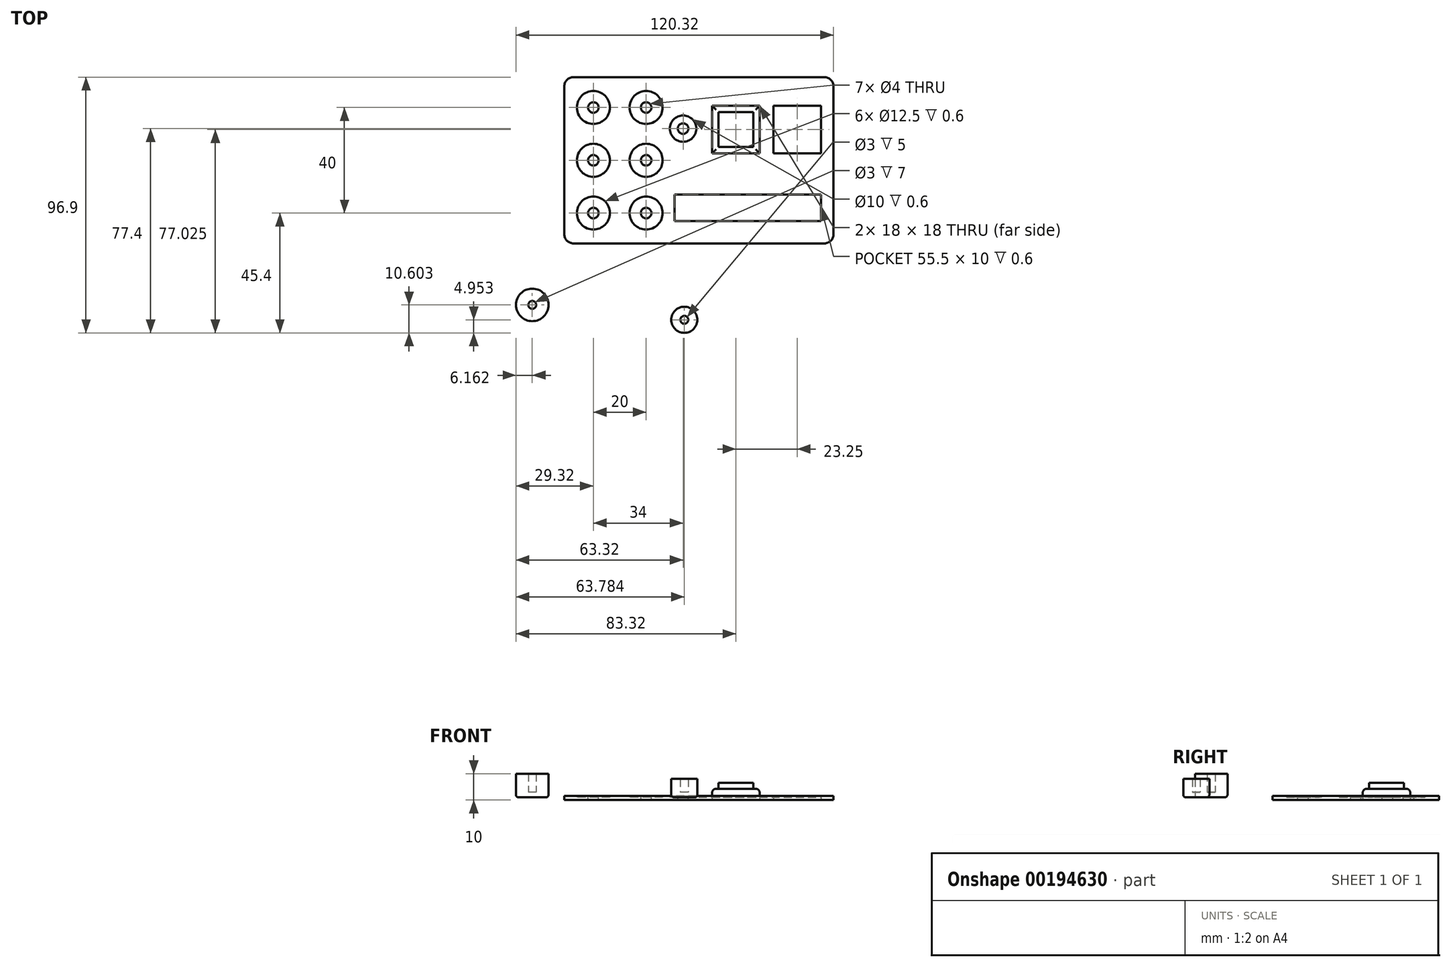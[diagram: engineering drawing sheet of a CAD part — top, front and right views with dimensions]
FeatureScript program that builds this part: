
annotation { "Feature Type Name" : "Feature", "Feature Type Description" : "" }
export const myFeature = defineFeature(function(context is Context, id is Id, definition is map)
    precondition{}
    {
        {
            var Q0;
            Q0=qCreatedBy(makeId("Top.planeOp"),FACE);
            var sketch = newSketch(context, id + "F0", { "sketchPlane" : qUnion([Q0])});
            skLineSegment(sketch, "E0.bottom", {"start": v(-47.5, 31.5) * mm, "end": v(47.5, 31.5) * mm});
            skLineSegment(sketch, "E0.top", {"start": v(-47.5, -31.5) * mm, "end": v(47.5, -31.5) * mm});
            skLineSegment(sketch, "E0.left", {"start": v(-51, 28) * mm, "end": v(-51, -28) * mm});
            skLineSegment(sketch, "E0.right", {"start": v(51, 28) * mm, "end": v(51, -28) * mm});
            skPoint(sketch, "E0.middle", {"position": v(0, 0) * mm});
            skLineSegment(sketch, "E1", {"start": v(-40, 40.5) * mm, "end": v(-40, -44.64) * mm, "construction": true});
            skLineSegment(sketch, "E2", {"start": v(-20, 44.64) * mm, "end": v(-20, -44.64) * mm, "construction": true});
            skLineSegment(sketch, "E3", {"start": v(-6, 41.7) * mm, "end": v(-6, -40.78) * mm, "construction": true});
            skLineSegment(sketch, "E4", {"start": v(66.95, 11.62) * mm, "end": v(16.06, 11.62) * mm, "construction": true});
            skLineSegment(sketch, "E5", {"start": v(14, 43.52) * mm, "end": v(14, 9.52) * mm, "construction": true});
            skLineSegment(sketch, "E6", {"start": v(37.25, 43.28) * mm, "end": v(37.25, 9.52) * mm, "construction": true});
            skLineSegment(sketch, "E7", {"start": v(37.25, 9.52) * mm, "end": v(37.73, 11.44) * mm, "construction": true});
            skLineSegment(sketch, "E8", {"start": v(-10.62, 12) * mm, "end": v(-2.9, 12) * mm, "construction": true});
            skLineSegment(sketch, "E9", {"start": v(-44.65, 20) * mm, "end": v(-19.09, 20) * mm, "construction": true});
            skLineSegment(sketch, "E10", {"start": v(-45.38, 0) * mm, "end": v(-19.09, 0) * mm, "construction": true});
            skLineSegment(sketch, "E11", {"start": v(-44.65, -20) * mm, "end": v(-19.09, -20) * mm, "construction": true});
            skPoint(sketch, "E12.visualSharp", {"position": v(-51, 31.5) * mm});
            skArc(sketch, "E12.filletArc", {"start": v(-47.5, 31.5) * mm, "mid": v(-49.97, 30.47) * mm, "end": v(-51, 28) * mm});
            skPoint(sketch, "E13.visualSharp", {"position": v(-51, -31.5) * mm});
            skArc(sketch, "E13.filletArc", {"start": v(-51, -28) * mm, "mid": v(-49.97, -30.47) * mm, "end": v(-47.5, -31.5) * mm});
            skPoint(sketch, "E14.visualSharp", {"position": v(51, -31.5) * mm});
            skArc(sketch, "E14.filletArc", {"start": v(47.5, -31.5) * mm, "mid": v(49.97, -30.47) * mm, "end": v(51, -28) * mm});
            skPoint(sketch, "E15.visualSharp", {"position": v(51, 31.5) * mm});
            skArc(sketch, "E15.filletArc", {"start": v(51, 28) * mm, "mid": v(49.97, 30.47) * mm, "end": v(47.5, 31.5) * mm});
            skCircle(sketch, "E16", {"center": v(-40, 20) * mm, "radius": 2 * mm});
            skCircle(sketch, "E17", {"center": v(-40, 20) * mm, "radius": 6.25 * mm});
            skCircle(sketch, "E18", {"center": v(-40, 0) * mm, "radius": 2 * mm});
            skCircle(sketch, "E19", {"center": v(-40, 0) * mm, "radius": 6.25 * mm});
            skCircle(sketch, "E20", {"center": v(-40, -20) * mm, "radius": 2 * mm});
            skCircle(sketch, "E21", {"center": v(-40, -20) * mm, "radius": 6.25 * mm});
            skCircle(sketch, "E22", {"center": v(-20, 20) * mm, "radius": 2 * mm});
            skCircle(sketch, "E23", {"center": v(-20, 20) * mm, "radius": 6.25 * mm});
            skCircle(sketch, "E24", {"center": v(-20, 0) * mm, "radius": 2 * mm});
            skCircle(sketch, "E25", {"center": v(-20, 0) * mm, "radius": 6.25 * mm});
            skCircle(sketch, "E26", {"center": v(-20, -20) * mm, "radius": 2 * mm});
            skCircle(sketch, "E27", {"center": v(-20, -20) * mm, "radius": 6.25 * mm});
            skCircle(sketch, "E28", {"center": v(-6, 12) * mm, "radius": 2 * mm});
            skCircle(sketch, "E29", {"center": v(-6, 12) * mm, "radius": 5 * mm});
            skLineSegment(sketch, "E30.bottom", {"start": v(7.38, 18.25) * mm, "end": v(20.62, 18.25) * mm});
            skLineSegment(sketch, "E30.top", {"start": v(7.37, 5) * mm, "end": v(20.62, 5) * mm});
            skLineSegment(sketch, "E30.left", {"start": v(7.38, 18.25) * mm, "end": v(7.37, 5) * mm});
            skLineSegment(sketch, "E30.right", {"start": v(20.62, 18.25) * mm, "end": v(20.62, 5) * mm});
            skPoint(sketch, "E30.middle", {"position": v(14, 11.63) * mm});
            skLineSegment(sketch, "E31.bottom", {"start": v(5, 20.63) * mm, "end": v(23, 20.63) * mm});
            skLineSegment(sketch, "E31.top", {"start": v(5, 2.63) * mm, "end": v(23, 2.63) * mm});
            skLineSegment(sketch, "E31.left", {"start": v(5, 20.63) * mm, "end": v(5, 2.63) * mm});
            skLineSegment(sketch, "E31.right", {"start": v(23, 20.63) * mm, "end": v(23, 2.63) * mm});
            skLineSegment(sketch, "E32.bottom", {"start": v(28.25, 20.63) * mm, "end": v(46.25, 20.63) * mm});
            skLineSegment(sketch, "E32.top", {"start": v(28.25, 2.63) * mm, "end": v(46.25, 2.63) * mm});
            skLineSegment(sketch, "E32.left", {"start": v(28.25, 20.63) * mm, "end": v(28.25, 2.63) * mm});
            skLineSegment(sketch, "E32.right", {"start": v(46.25, 20.63) * mm, "end": v(46.25, 2.63) * mm});
            skPoint(sketch, "E32.middle", {"position": v(37.25, 11.63) * mm});
            skLineSegment(sketch, "E33.bottom", {"start": v(30.62, 18.25) * mm, "end": v(43.88, 18.25) * mm});
            skLineSegment(sketch, "E33.top", {"start": v(30.62, 5) * mm, "end": v(43.88, 5) * mm});
            skLineSegment(sketch, "E33.left", {"start": v(30.62, 18.25) * mm, "end": v(30.62, 5) * mm});
            skLineSegment(sketch, "E33.right", {"start": v(43.88, 18.25) * mm, "end": v(43.88, 5) * mm});
            skPoint(sketch, "E34", {"position": v(18.5, -18) * mm});
            skLineSegment(sketch, "E35.bottom", {"start": v(-9.25, -13) * mm, "end": v(46.25, -13) * mm});
            skLineSegment(sketch, "E35.top", {"start": v(-9.25, -23) * mm, "end": v(46.25, -23) * mm});
            skLineSegment(sketch, "E35.left", {"start": v(-9.25, -13) * mm, "end": v(-9.25, -23) * mm});
            skLineSegment(sketch, "E35.right", {"start": v(46.25, -13) * mm, "end": v(46.25, -23) * mm});
            skSolve(sketch);
        }
        {
            var Q0;
            Q0=makeQuery(id+"F0.imprint","IMPRINT",FACE,{"disambiguationData":[TD([[makeQuery(id+"F0.imprint","IMPRINT",EDGE,{"derivedFrom":sQuery(id+"F0.wireOp",EDGE,"E0.bottom")}),-1.0]])]});
            extrude(context, id + "F1", {"entities" : qUnion([Q0]), "depth" : .6 * mm});
        }
        {
            var Q0;
            Q0=makeQuery(id+"F0.imprint","IMPRINT",FACE,{"disambiguationData":[TD([[makeQuery(id+"F0.imprint","IMPRINT",EDGE,{"derivedFrom":sQuery(id+"F0.wireOp",EDGE,"E0.bottom")}),-1.0]])]});
            var Q1;
            Q1=makeQuery(id+"F0.imprint","IMPRINT",FACE,{"disambiguationData":[TD([[makeQuery(id+"F0.imprint","IMPRINT",EDGE,{"derivedFrom":sQuery(id+"F0.wireOp",EDGE,"E20")}),-1.0]])]});
            var Q2;
            Q2=makeQuery(id+"F0.imprint","IMPRINT",FACE,{"disambiguationData":[TD([[makeQuery(id+"F0.imprint","IMPRINT",EDGE,{"derivedFrom":sQuery(id+"F0.wireOp",EDGE,"E18")}),-1.0]])]});
            var Q3;
            Q3=makeQuery(id+"F0.imprint","IMPRINT",FACE,{"disambiguationData":[TD([[makeQuery(id+"F0.imprint","IMPRINT",EDGE,{"derivedFrom":sQuery(id+"F0.wireOp",EDGE,"E16")}),-1.0]])]});
            var Q4;
            Q4=makeQuery(id+"F0.imprint","IMPRINT",FACE,{"disambiguationData":[TD([[makeQuery(id+"F0.imprint","IMPRINT",EDGE,{"derivedFrom":sQuery(id+"F0.wireOp",EDGE,"E22")}),-1.0]])]});
            var Q5;
            Q5=makeQuery(id+"F0.imprint","IMPRINT",FACE,{"disambiguationData":[TD([[makeQuery(id+"F0.imprint","IMPRINT",EDGE,{"derivedFrom":sQuery(id+"F0.wireOp",EDGE,"E24")}),-1.0]])]});
            var Q6;
            Q6=makeQuery(id+"F0.imprint","IMPRINT",FACE,{"disambiguationData":[TD([[makeQuery(id+"F0.imprint","IMPRINT",EDGE,{"derivedFrom":sQuery(id+"F0.wireOp",EDGE,"E26")}),-1.0]])]});
            var Q7;
            Q7=makeQuery(id+"F0.imprint","IMPRINT",FACE,{"disambiguationData":[TD([[makeQuery(id+"F0.imprint","IMPRINT",EDGE,{"derivedFrom":sQuery(id+"F0.wireOp",EDGE,"E28")}),-1.0]])]});
            var Q8;
            Q8=makeQuery(id+"F0.imprint","IMPRINT",FACE,{"disambiguationData":[TD([[makeQuery(id+"F0.imprint","IMPRINT",EDGE,{"derivedFrom":sQuery(id+"F0.wireOp",EDGE,"E35.bottom")}),-1.0]])]});
            extrude(context, id + "F2", {"entities" : qUnion([Q0, Q1, Q2, Q3, Q4, Q5, Q6, Q7, Q8]), "operationType" : NewBodyOperationType.ADD, "oppositeDirection" : true, "depth" : 1 * mm});
        }
        {
            var Q0;
            Q0=makeQuery(id+"F0.imprint","IMPRINT",FACE,{"disambiguationData":[TD([[makeQuery(id+"F0.imprint","IMPRINT",EDGE,{"derivedFrom":sQuery(id+"F0.wireOp",EDGE,"E30.bottom")}),-1.0]])]});
            var Q1;
            Q1=makeQuery(id+"F0.imprint","IMPRINT",FACE,{"disambiguationData":[TD([[makeQuery(id+"F0.imprint","IMPRINT",EDGE,{"derivedFrom":sQuery(id+"F0.wireOp",EDGE,"E30.bottom")}),1.0]])]});
            extrude(context, id + "F3", {"entities" : qUnion([Q0, Q1]), "depth" : 3.3 * mm});
        }
        {
            var Q0;
            Q0=makeQuery(id+"F0.imprint","IMPRINT",FACE,{"disambiguationData":[TD([[makeQuery(id+"F0.imprint","IMPRINT",EDGE,{"derivedFrom":sQuery(id+"F0.wireOp",EDGE,"E30.bottom")}),-1.0]])]});
            extrude(context, id + "F4", {"entities" : qUnion([Q0]), "operationType" : NewBodyOperationType.ADD, "depth" : 5.5 * mm});
        }
        {
            var Q0;
            Q0=makeQuery(id+"F3.opExtrude","CAP_EDGE",EDGE,{"disambiguationData":[OSD([sQuery(id+"F0.wireOp",EDGE,"E31.top")])],"isStart":false});
            var Q1;
            Q1=makeQuery(id+"F3.opExtrude","CAP_EDGE",EDGE,{"disambiguationData":[OSD([sQuery(id+"F0.wireOp",EDGE,"E31.right")])],"isStart":false});
            var Q2;
            Q2=makeQuery(id+"F3.opExtrude","CAP_EDGE",EDGE,{"disambiguationData":[OSD([sQuery(id+"F0.wireOp",EDGE,"E31.bottom")])],"isStart":false});
            var Q3;
            Q3=makeQuery(id+"F3.opExtrude","CAP_EDGE",EDGE,{"disambiguationData":[OSD([sQuery(id+"F0.wireOp",EDGE,"E31.left")])],"isStart":false});
            fillet(context, id + "F5", {"entities" : qUnion([Q0, Q1, Q2, Q3]), "radius" : 1.5 * mm, "tangentPropagation" : true, "allowEdgeOverflow" : false});
        }
        {
            var Q0;
            Q0=qCreatedBy(makeId("Top.planeOp"),FACE);
            var sketch = newSketch(context, id + "F6", { "sketchPlane" : qUnion([Q0])});
            skCircle(sketch, "E36", {"center": v(-63.16, -54.8) * mm, "radius": 6.17 * mm});
            skCircle(sketch, "E37", {"center": v(-63.16, -54.8) * mm, "radius": 1.5 * mm});
            skCircle(sketch, "E38", {"center": v(-5.54, -60.45) * mm, "radius": 4.95 * mm});
            skCircle(sketch, "E39", {"center": v(-5.54, -60.45) * mm, "radius": 1.5 * mm});
            skSolve(sketch);
        }
        {
            var Q0;
            Q0=makeQuery(id+"F6.imprint","IMPRINT",FACE,{"disambiguationData":[TD([[makeQuery(id+"F6.imprint","IMPRINT",EDGE,{"derivedFrom":sQuery(id+"F6.wireOp",EDGE,"E36")}),1.0]])]});
            var Q1;
            Q1=sQuery(id+"F6.wireOp",EDGE,"E36");
            extrude(context, id + "F7", {"entities" : qUnion([Q0]), "surfaceEntities" : qUnion([Q1]), "depth" : 9 * mm});
        }
        {
            var Q0;
            Q0=makeQuery(id+"F6.imprint","IMPRINT",FACE,{"disambiguationData":[TD([[makeQuery(id+"F6.imprint","IMPRINT",EDGE,{"derivedFrom":sQuery(id+"F6.wireOp",EDGE,"E36")}),1.0]])]});
            var Q1;
            Q1=makeQuery(id+"F6.imprint","IMPRINT",FACE,{"disambiguationData":[TD([[makeQuery(id+"F6.imprint","IMPRINT",EDGE,{"derivedFrom":sQuery(id+"F6.wireOp",EDGE,"E37")}),1.0]])]});
            extrude(context, id + "F8", {"entities" : qUnion([Q0, Q1]), "operationType" : NewBodyOperationType.ADD, "depth" : 2 * mm});
        }
        {
            var Q0;
            Q0=makeQuery(id+"F7.opExtrude","CAP_EDGE",EDGE,{"disambiguationData":[OSD([sQuery(id+"F6.wireOp",EDGE,"E36")])],"isStart":true});
            fillet(context, id + "F9", {"entities" : qUnion([Q0]), "radius" : 1 * mm, "tangentPropagation" : true, "allowEdgeOverflow" : false});
        }
        {
            var Q0;
            Q0=makeQuery(id+"F6.imprint","IMPRINT",FACE,{"disambiguationData":[TD([[makeQuery(id+"F6.imprint","IMPRINT",EDGE,{"derivedFrom":sQuery(id+"F6.wireOp",EDGE,"E38")}),1.0]])]});
            extrude(context, id + "F10", {"entities" : qUnion([Q0]), "depth" : 7 * mm});
        }
        {
            var Q0;
            Q0=makeQuery(id+"F6.imprint","IMPRINT",FACE,{"disambiguationData":[TD([[makeQuery(id+"F6.imprint","IMPRINT",EDGE,{"derivedFrom":sQuery(id+"F6.wireOp",EDGE,"E38")}),1.0]])]});
            var Q1;
            Q1=makeQuery(id+"F6.imprint","IMPRINT",FACE,{"disambiguationData":[TD([[makeQuery(id+"F6.imprint","IMPRINT",EDGE,{"derivedFrom":sQuery(id+"F6.wireOp",EDGE,"E39")}),1.0]])]});
            extrude(context, id + "F11", {"entities" : qUnion([Q0, Q1]), "operationType" : NewBodyOperationType.ADD, "depth" : 2 * mm});
        }
        {
            var Q0;
            Q0=makeQuery(id+"F10.opExtrude","CAP_EDGE",EDGE,{"disambiguationData":[OSD([sQuery(id+"F6.wireOp",EDGE,"E38")])],"isStart":true});
            fillet(context, id + "F12", {"entities" : qUnion([Q0]), "radius" : 1 * mm, "tangentPropagation" : true, "allowEdgeOverflow" : false});
        }
    });
